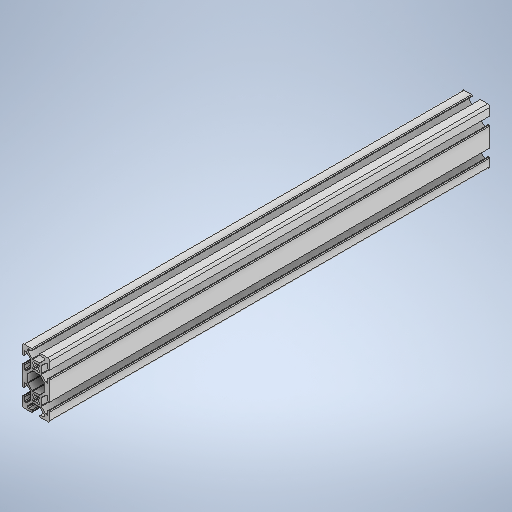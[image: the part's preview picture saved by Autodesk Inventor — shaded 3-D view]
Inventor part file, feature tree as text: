
AUTODESK INVENTOR PART (.ipt)
format: ipt  version: 2025 (Build 290162000, 162)  size: 484,352 bytes
history: native  units: in
note: dims shown in document units (in); Inventor stores cm internally (conversion verified against a paired STEP export)
features: extrude x1, sketch x1
ambient origin geometry x8: Origin, YZ Plane, XZ Plane, XY Plane, X Axis, Y Axis, Z Axis, Center Point
bodies: Solid1 (feature_tree)
feature tree (2):
  extrude  "Extrusion1"  [1 undecoded]
  sketch  "Sketch1"  dims[d0=12.5in d1=0.0in]
note: 1 required parameter value undecoded (feature->parameter linkage not recoverable at this tier; creation-order binding heuristic only, values carry confidence <= 0.55)
